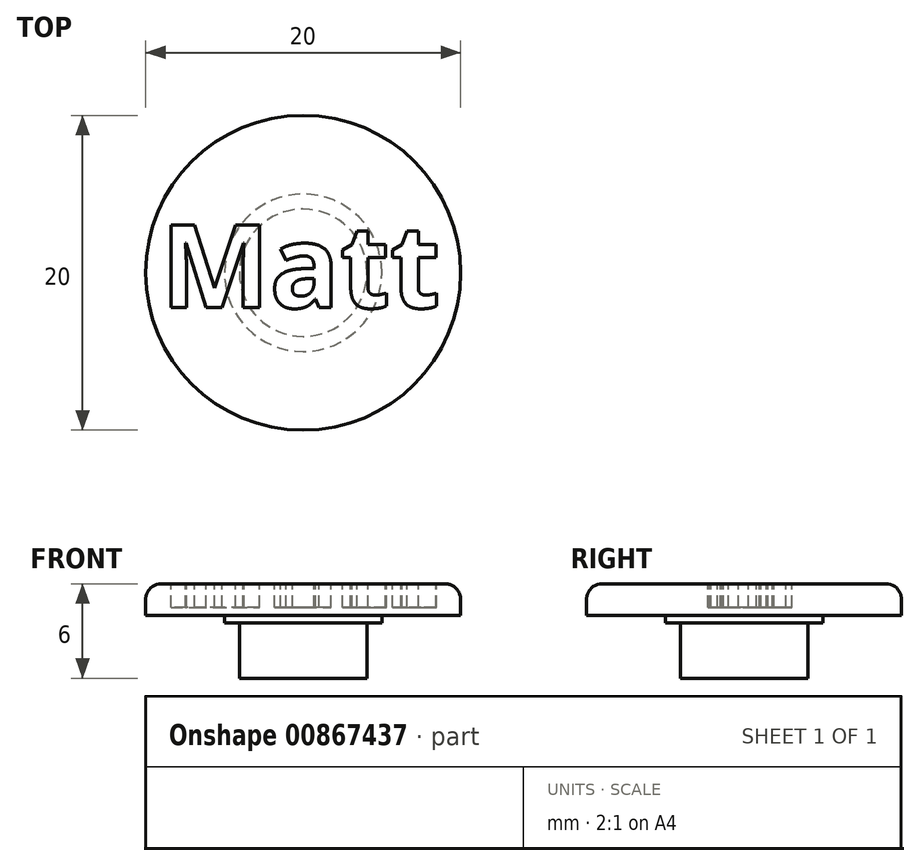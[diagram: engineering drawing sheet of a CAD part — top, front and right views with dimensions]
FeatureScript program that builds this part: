
annotation { "Feature Type Name" : "Feature", "Feature Type Description" : "" }
export const myFeature = defineFeature(function(context is Context, id is Id, definition is map)
    precondition{}
    {
        {
            var Q0;
            Q0=qCreatedBy(makeId("Top.planeOp"),FACE);
            var sketch = newSketch(context, id + "F0", { "sketchPlane" : qUnion([Q0])});
            skCircle(sketch, "E0", {"center": v(0, 0) * mm, "radius": 10 * mm});
            skCircle(sketch, "E1", {"center": v(0, 0) * mm, "radius": 4.05 * mm});
            skCircle(sketch, "E2", {"center": v(0, 0) * mm, "radius": 5 * mm});
            skSolve(sketch);
        }
        {
            var Q0;
            Q0=makeQuery(id+"F0.imprint","IMPRINT",FACE,{"disambiguationData":[TD([[makeQuery(id+"F0.imprint","IMPRINT",EDGE,{"derivedFrom":sQuery(id+"F0.wireOp",EDGE,"E1")}),1.0]])]});
            extrude(context, id + "F1", {"entities" : qUnion([Q0]), "oppositeDirection" : true, "depth" : 6 * mm, "offsetDistance" : 25 * mm});
        }
        {
            var Q0;
            Q0=makeQuery(id+"F0.imprint","IMPRINT",FACE,{"disambiguationData":[TD([[makeQuery(id+"F0.imprint","IMPRINT",EDGE,{"derivedFrom":sQuery(id+"F0.wireOp",EDGE,"E1")}),-1.0]])]});
            extrude(context, id + "F2", {"entities" : qUnion([Q0]), "operationType" : NewBodyOperationType.ADD, "oppositeDirection" : true, "depth" : 2.5 * mm, "offsetDistance" : 25 * mm});
        }
        {
            var Q0;
            Q0=makeQuery(id+"F0.imprint","IMPRINT",FACE,{"disambiguationData":[TD([[makeQuery(id+"F0.imprint","IMPRINT",EDGE,{"derivedFrom":sQuery(id+"F0.wireOp",EDGE,"E0")}),1.0]])]});
            extrude(context, id + "F3", {"entities" : qUnion([Q0]), "operationType" : NewBodyOperationType.ADD, "oppositeDirection" : true, "depth" : 2 * mm, "offsetDistance" : 25 * mm});
        }
        {
            var Q0;
            Q0=makeQuery(id+"F3.opExtrude","CAP_EDGE",EDGE,{"disambiguationData":[OSD([sQuery(id+"F0.wireOp",EDGE,"E0")])],"isStart":true});
            fillet(context, id + "F4", {"entities" : qUnion([Q0]), "radius" : 1 * mm, "tangentPropagation" : true, "allowEdgeOverflow" : false});
        }
        {
            var Q0;
            Q0=qCreatedBy(makeId("Top.planeOp"),FACE);
            var sketch = newSketch(context, id + "F5", { "sketchPlane" : qUnion([Q0])});
            skText(sketch, "E3", { "text": "Matt", "fontName": "OpenSans-Bold.ttf"});
            const initialGuessF5  = {"E3": [-0.00906, -0.00222, 1, 0, 0.0053]};
            skSetInitialGuess(sketch, initialGuessF5);
            skSolve(sketch);
        }
        {
            var Q0;
            Q0 = qSketchRegion(id + "F5", true);
            extrude(context, id + "F6", {"entities" : qUnion([Q0]), "operationType" : NewBodyOperationType.REMOVE, "oppositeDirection" : true, "depth" : 1.5 * mm, "offsetDistance" : 25 * mm});
        }
    });
